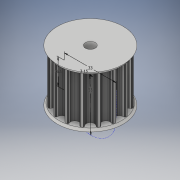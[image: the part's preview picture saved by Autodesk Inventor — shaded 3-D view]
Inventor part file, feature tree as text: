
AUTODESK INVENTOR PART (.ipt)
format: ipt  version: 2019 (Build 230136000, 136)  size: 1,654,784 bytes
history: native  units: mm
features: sketch x13, extrude x7, plane x6, loft x2, hole x1
ambient origin geometry x8: Origin, YZ Plane, XZ Plane, XY Plane, X Axis, Y Axis, Z Axis, Center Point
bodies: Solid1 (feature_tree)
feature tree (29):
  extrude  "Extrusion1"  Depth=30.0mm
  sketch  "Sketch2"  dims[d3=1.5mm d4=42.0mm]
  plane  "Work Plane1"
  loft  "Loft1"
  sketch  "Sketch4"  dims[d9=40.0mm d10=1.5mm]
  plane  "Work Plane2"
  loft  "Loft2"
  hole  "Hole1"  [1 undecoded]
  extrude  "Extrusion2"  TaperAngle=0.0deg  [1 undecoded]
  plane  "Work Plane3"
  extrude  "Extrusion3"  Depth=33.0mm
  extrude  "Extrusion4"  Depth=33.0mm
  plane  "Work Plane4"
  extrude  "Extrusion5"  Depth=30.0mm TaperAngle=0.0deg
  sketch  "Sketch13"  dims[d31=4.0mm d32=2.5mm d33=0.0mm d34=0.0mm d35=33.0mm]
  plane  "Work Plane5"
  extrude  "Extrusion6"  Depth=6.0mm
  plane  "Work Plane6"
  extrude  "Extrusion7"  Depth=33.0mm
  sketch  "Sketch1"  dims[d0=30.0mm d1=0.0mm d2=40.0mm]
  sketch  "Sketch3"  dims[d5=0.0mm d6=90.0deg d7=0.0mm d8=90.0deg]
  sketch  "Sketch5"  dims[d11=42.0mm d12=0.0mm d13=90.0deg]
  sketch  "Sketch6"  dims[d14=0.0mm d15=90.0deg]
  sketch  "Sketch8"  dims[d16=6.28mm d17=6.0mm d18=15.0mm d19=7.0mm d20=90.0deg d21=8.0mm d22=20.594885mm d23=33.0mm]
  sketch  "Sketch10"  dims[d24=33.0mm d25=16.5mm]
  sketch  "Sketch11"  dims[d26=3.15mm d27=30.0mm d28=0.0mm]
  sketch  "Sketch12"  dims[d29=-16.75mm d30=6.0mm]
  sketch  "Sketch14"  dims[d36=16.5mm]
  sketch  "Sketch15"  dims[d37=33.0mm d38=3.15mm d39=6.0mm d40=0.0mm d41=-16.5mm d42=6.0mm d43=3.0mm d44=5.0mm d45=0.0mm d46=0.0mm d47=6.0mm d48=6.0mm d49=15.0mm d50=2.35mm d51=0.0mm d52=6.0mm d53=15.0mm d54=6.0mm d55=2.35mm d56=0.0mm]
note: 2 required parameter values undecoded (feature->parameter linkage not recoverable at this tier; creation-order binding heuristic only, values carry confidence <= 0.55)
